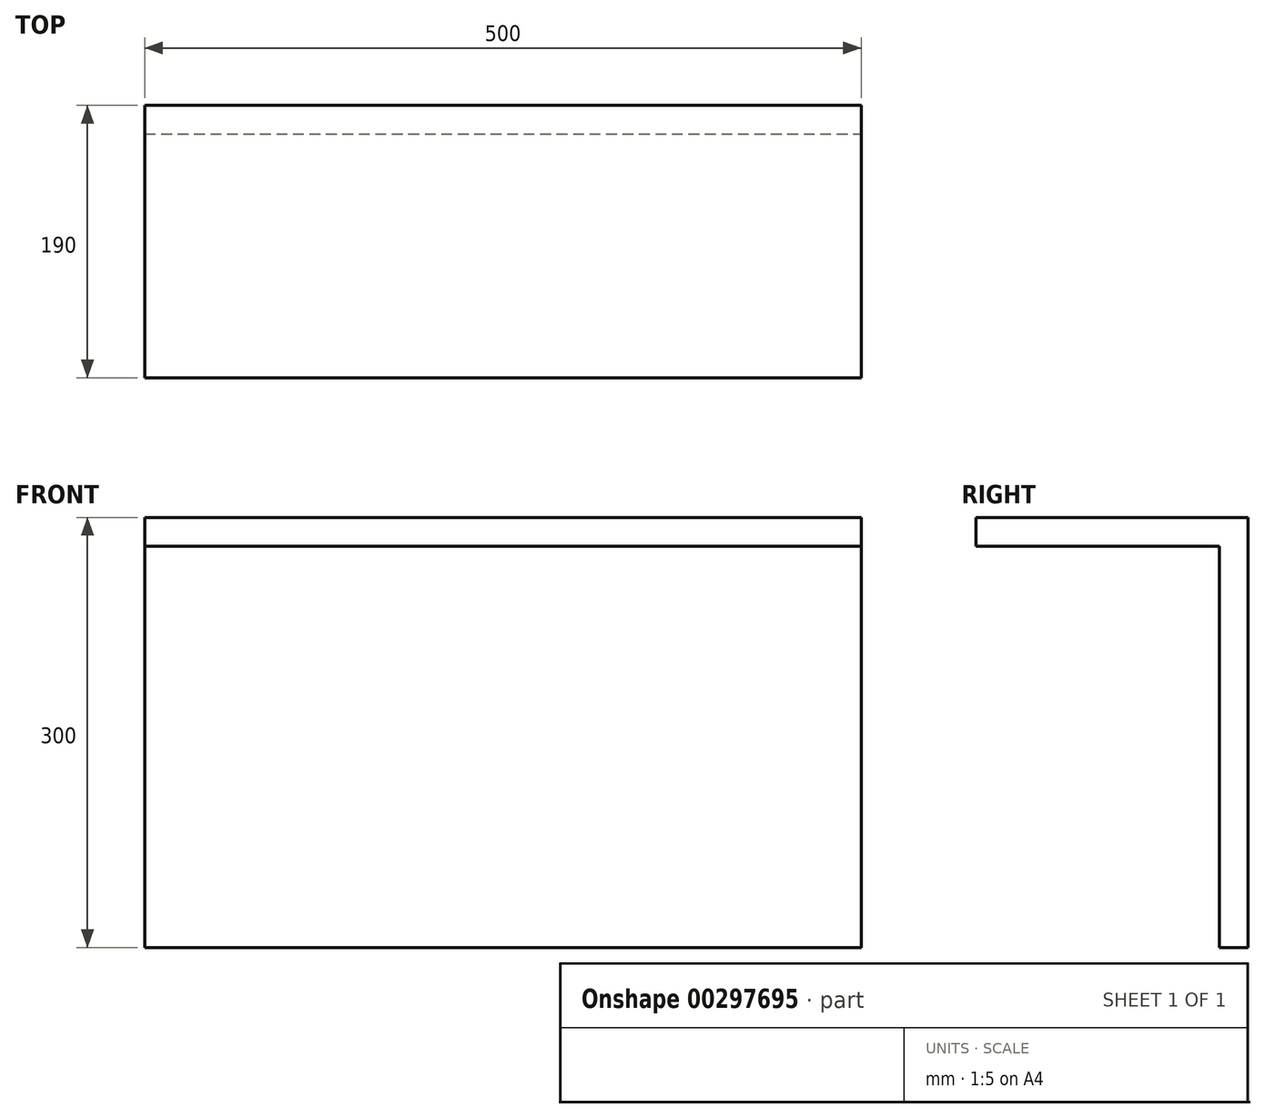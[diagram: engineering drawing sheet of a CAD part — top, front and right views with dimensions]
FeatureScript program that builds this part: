
annotation { "Feature Type Name" : "Feature", "Feature Type Description" : "" }
export const myFeature = defineFeature(function(context is Context, id is Id, definition is map)
    precondition{}
    {
        {
            var Q0;
            Q0=qCreatedBy(makeId("Top.planeOp"),FACE);
            var sketch = newSketch(context, id + "F0", { "sketchPlane" : qUnion([Q0])});
            skLineSegment(sketch, "E0", {"start": v(0, 0) * mm, "end": v(250, 0) * mm, "construction": true});
            skLineSegment(sketch, "E1.bottom", {"start": v(250, 0) * mm, "end": v(-250, 0) * mm});
            skLineSegment(sketch, "E1.top", {"start": v(250, -190) * mm, "end": v(-250, -190) * mm});
            skLineSegment(sketch, "E1.left", {"start": v(250, 0) * mm, "end": v(250, -190) * mm});
            skLineSegment(sketch, "E1.right", {"start": v(-250, 0) * mm, "end": v(-250, -190) * mm});
            skSolve(sketch);
        }
        {
            var Q0;
            Q0=makeQuery(id+"F0.imprint","IMPRINT",FACE,{"disambiguationData":[TD([[makeQuery(id+"F0.imprint","IMPRINT",EDGE,{"derivedFrom":sQuery(id+"F0.wireOp",EDGE,"E1.bottom")}),1.0]])]});
            extrude(context, id + "F1", {"entities" : qUnion([Q0]), "oppositeDirection" : true, "depth" : 20 * mm});
        }
        {
            var Q0;
            Q0=qCreatedBy(makeId("Front.planeOp"),FACE);
            var sketch = newSketch(context, id + "F2", { "sketchPlane" : qUnion([Q0])});
            skLineSegment(sketch, "E2", {"start": v(0, 0) * mm, "end": v(0, -300) * mm, "construction": true});
            skLineSegment(sketch, "E3", {"start": v(0, -300) * mm, "end": v(250, -300) * mm, "construction": true});
            skLineSegment(sketch, "E4", {"start": v(0, 0) * mm, "end": v(-250, 0) * mm, "construction": true});
            skLineSegment(sketch, "E5.bottom", {"start": v(250, -300) * mm, "end": v(-250, -300) * mm});
            skLineSegment(sketch, "E5.top", {"start": v(250, 0) * mm, "end": v(-250, 0) * mm});
            skLineSegment(sketch, "E5.left", {"start": v(250, -300) * mm, "end": v(250, 0) * mm});
            skLineSegment(sketch, "E5.right", {"start": v(-250, -300) * mm, "end": v(-250, 0) * mm});
            skSolve(sketch);
        }
        {
            var Q0;
            Q0=makeQuery(id+"F2.imprint","IMPRINT",FACE,{"disambiguationData":[TD([[makeQuery(id+"F2.imprint","IMPRINT",EDGE,{"derivedFrom":sQuery(id+"F2.wireOp",EDGE,"E5.bottom")}),-1.0]])]});
            extrude(context, id + "F3", {"entities" : qUnion([Q0]), "operationType" : NewBodyOperationType.ADD, "depth" : 20 * mm});
        }
        {
            var Q0;
            Q0=makeQuery(id+"F3.opExtrude","CAP_FACE",FACE,{"disambiguationData":[OSD([sQuery(id+"F2.wireOp",EDGE,"E5.bottom"),sQuery(id+"F2.wireOp",EDGE,"E5.top"),sQuery(id+"F2.wireOp",EDGE,"E5.left"),sQuery(id+"F2.wireOp",EDGE,"E5.right")])],"isStart":false});
            var sketch = newSketch(context, id + "F4", { "sketchPlane" : qUnion([Q0])});
            skPoint(sketch, "E6.endSnap0", {"position": v(0, -20) * mm});
            skLineSegment(sketch, "E7", {"start": v(0, -20) * mm, "end": v(0, -150) * mm, "construction": true});
            skLineSegment(sketch, "E8.bottom", {"start": v(-250, -160) * mm, "end": v(250, -160) * mm});
            skLineSegment(sketch, "E8.top", {"start": v(-250, -140) * mm, "end": v(250, -140) * mm});
            skLineSegment(sketch, "E8.left", {"start": v(-250, -160) * mm, "end": v(-250, -140) * mm});
            skLineSegment(sketch, "E8.right", {"start": v(250, -160) * mm, "end": v(250, -140) * mm});
            skPoint(sketch, "E8.middle", {"position": v(0, -150) * mm});
            skSolve(sketch);
        }
        {
            var Q0;
            Q0=sQuery(id+"F4.wireOp",EDGE,"E8.top");
            var Q1;
            Q1=sQuery(id+"F4.wireOp",EDGE,"E8.left");
            var Q2;
            Q2=sQuery(id+"F4.wireOp",EDGE,"E8.bottom");
            var Q3;
            Q3=sQuery(id+"F4.wireOp",EDGE,"E8.right");
            extrude(context, id + "F5", {"bodyType" : ExtendedToolBodyType.SURFACE, "surfaceEntities" : qUnion([Q0, Q1, Q2, Q3]), "depth" : 170 * mm});
        }
        {
            var Q0;
            {var subQ0=sQuery(id+"F4.wireOp",EDGE,"E8.top");Q0=makeQuery(id+"F4.imprint","IMPRINT",FACE,{"disambiguationData":[TD([[makeQuery(id+"F4.imprint","IMPRINT",EDGE,{"derivedFrom":subQ0}),1.0]])]});}
            var sketch = newSketch(context, id + "F6", { "sketchPlane" : qUnion([Q0])});
            skLineSegment(sketch, "E9", {"start": v(-230, -20) * mm, "end": v(0, -20) * mm, "construction": true});
            skLineSegment(sketch, "E10", {"start": v(0, -20) * mm, "end": v(230, -20) * mm, "construction": true});
            skLineSegment(sketch, "E11.bottom", {"start": v(-230, -20) * mm, "end": v(-250, -20) * mm});
            skLineSegment(sketch, "E11.top", {"start": v(-230, -140) * mm, "end": v(-250, -140) * mm});
            skLineSegment(sketch, "E11.left", {"start": v(-230, -20) * mm, "end": v(-230, -140) * mm});
            skLineSegment(sketch, "E11.right", {"start": v(-250, -20) * mm, "end": v(-250, -140) * mm});
            skLineSegment(sketch, "E12.bottom", {"start": v(230, -20) * mm, "end": v(250, -20) * mm});
            skLineSegment(sketch, "E12.top", {"start": v(230, -140) * mm, "end": v(250, -140) * mm});
            skLineSegment(sketch, "E12.left", {"start": v(230, -20) * mm, "end": v(230, -140) * mm});
            skLineSegment(sketch, "E12.right", {"start": v(250, -20) * mm, "end": v(250, -140) * mm});
            skSolve(sketch);
        }
        {
            var Q0;
            Q0=sQuery(id+"F6.wireOp",EDGE,"E11.right");
            var Q1;
            Q1=sQuery(id+"F6.wireOp",EDGE,"E11.left");
            var Q2;
            Q2=sQuery(id+"F6.wireOp",EDGE,"E11.bottom");
            var Q3;
            Q3=sQuery(id+"F6.wireOp",EDGE,"E11.top");
            var Q4;
            Q4=sQuery(id+"F6.wireOp",EDGE,"E12.left");
            var Q5;
            Q5=sQuery(id+"F6.wireOp",EDGE,"E12.right");
            var Q6;
            Q6=sQuery(id+"F6.wireOp",EDGE,"E12.bottom");
            var Q7;
            Q7=sQuery(id+"F6.wireOp",EDGE,"E12.top");
            extrude(context, id + "F7", {"bodyType" : ExtendedToolBodyType.SURFACE, "surfaceEntities" : qUnion([Q0, Q1, Q2, Q3, Q4, Q5, Q6, Q7]), "depth" : 170 * mm});
        }
        {
            var Q0;
            {var subQ0=sQuery(id+"F4.wireOp",EDGE,"E8.top");Q0=makeQuery(id+"F4.imprint","IMPRINT",FACE,{"disambiguationData":[TD([[makeQuery(id+"F4.imprint","IMPRINT",EDGE,{"derivedFrom":subQ0}),1.0]])]});}
            var sketch = newSketch(context, id + "F8", { "sketchPlane" : qUnion([Q0])});
            skLineSegment(sketch, "E13", {"start": v(-10, -20) * mm, "end": v(0, -20) * mm, "construction": true});
            skLineSegment(sketch, "E14.bottom", {"start": v(-10, -20) * mm, "end": v(10, -20) * mm});
            skLineSegment(sketch, "E14.top", {"start": v(-10, -140) * mm, "end": v(10, -140) * mm});
            skLineSegment(sketch, "E14.left", {"start": v(-10, -20) * mm, "end": v(-10, -140) * mm});
            skLineSegment(sketch, "E14.right", {"start": v(10, -20) * mm, "end": v(10, -140) * mm});
            skSolve(sketch);
        }
        {
            var Q0;
            Q0=sQuery(id+"F8.wireOp",EDGE,"E14.left");
            var Q1;
            Q1=sQuery(id+"F8.wireOp",EDGE,"E14.right");
            var Q2;
            Q2=sQuery(id+"F8.wireOp",EDGE,"E14.top");
            var Q3;
            Q3=sQuery(id+"F8.wireOp",EDGE,"E14.bottom");
            extrude(context, id + "F9", {"bodyType" : ExtendedToolBodyType.SURFACE, "surfaceEntities" : qUnion([Q0, Q1, Q2, Q3]), "depth" : 170 * mm});
        }
    });
